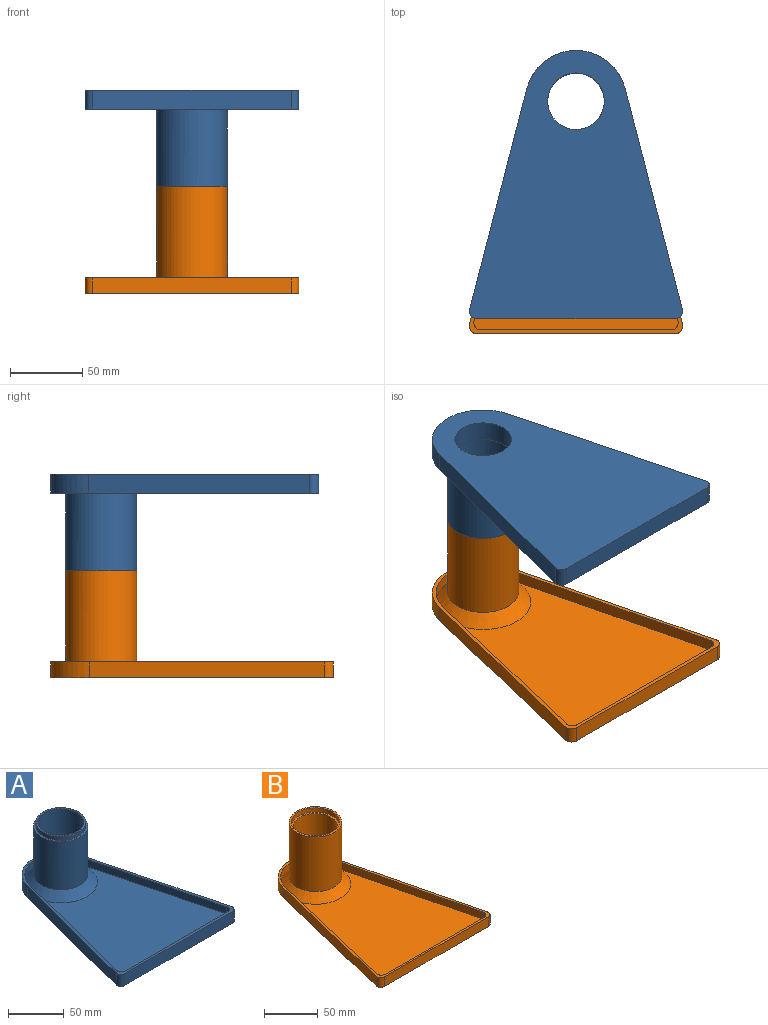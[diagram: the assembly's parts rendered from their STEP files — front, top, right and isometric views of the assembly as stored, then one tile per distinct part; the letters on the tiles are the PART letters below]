
ASSEMBLY  parts=2 mates=1
PART A: 25 faces, bbox 147.1x185x71 mm
  f0: plane 44.55x44.55mm, normal (0,0,1), area 196.3mm2, adj f19,f20
  f1: cylinder r=24.5mm len=53mm, axis (0,0,-1), area 8158.7mm2, adj f16,f17
  f2: plane 41.15x41.15mm, normal (0,0,1), area 135.3mm2, adj f14,f15
  f3: plane 152.52x39.5mm, normal (-0.97,0.25,0), area 2048.2mm2, adj f6,f7,f12,f23
  f4: plane 137.08x13mm, normal (0,-1,0), area 1782mm2, adj f7,f12,f23,f24
  f5: plane 152.52x39.5mm, normal (0.97,0.25,0), area 2048.2mm2, adj f6,f7,f12,f24
  f6: cylinder r=35mm len=67.76mm, axis (0,0,-1), area 1198.8mm2, adj f3,f5,f7,f12
  f7: plane 185x147.08mm, normal (0,0,-1), area 17390.7mm2, adj f3,f4,f5,f6,f14,f23,f24
  f8: plane 149.39x38.69mm, normal (-0.97,-0.25,0), area 1232.7mm2, adj f11,f12,f13,f16,f21
  f9: plane 130.62x8mm, normal (0,1,0), area 1045mm2, adj f12,f13,f21,f22
  f10: plane 149.39x38.69mm, normal (0.97,-0.25,0), area 1232.7mm2, adj f11,f12,f13,f16,f22
  f11: cylinder r=32.5mm len=62.92mm, axis (0,0,-1), area 642.2mm2, adj f8,f10,f12,f16
  f12: plane 185x147.08mm, normal (0,0,1), area 1401.2mm2, adj f3,f4,f5,f6,f8,f9,f10,f11
  f13: plane 150.11x140.62mm, normal (0,0,1), area 13809.8mm2, adj f8,f9,f10,f16,f21,f22
  f14: cylinder r=19.5mm len=39mm, axis (0,0,-1), area 1715.3mm2, adj f2,f7
  f15: cylinder r=20.57mm len=56.75mm, axis (0,0,-1), area 7336.4mm2, adj f2,f19
  f16: cone r=24.5mm half-angle=45deg, axis (0,0,-1), area 2105mm2, adj f1,f8,f10,f11,f13
  f17: plane 49x49mm, normal (0,0,1), area 291.8mm2, adj f1,f18
  f18: cylinder r=22.52mm len=45.05mm, axis (0,0,1), area 601.5mm2, adj f17,f20
  f19: cone r=20.57mm half-angle=45deg, axis (0,0,1), area 46mm2, adj f0,f15
  f20: cone r=22.27mm half-angle=45deg, axis (0,0,-1), area 49.8mm2, adj f0,f18
  f21: cylinder r=5mm len=8mm, axis (0,0,1), area 73mm2, adj f8,f9,f12,f13
  f22: cylinder r=5mm len=8mm, axis (0,0,-1), area 73mm2, adj f9,f10,f12,f13
  f23: cylinder r=5mm len=13mm, axis (0,0,1), area 118.6mm2, adj f3,f4,f7,f12
  f24: cylinder r=5mm len=13mm, axis (0,0,-1), area 118.6mm2, adj f4,f5,f7,f12
PART B: 23 faces, bbox 147.3x195x74 mm
  f0: plane 41.15x41.15mm, normal (0,0,1), area 135.3mm2, adj f12,f17
  f1: plane 162.1x39.49mm, normal (-0.97,0.24,0), area 1835.2mm2, adj f4,f5,f10,f21
  f2: plane 137.27x11mm, normal (0,-1,0), area 1510mm2, adj f5,f10,f21,f22
  f3: plane 162.1x39.49mm, normal (0.97,0.24,0), area 1835.2mm2, adj f4,f5,f10,f22
  f4: cylinder r=35mm len=68.01mm, axis (0,0,-1), area 1025.5mm2, adj f1,f3,f5,f10
  f5: plane 195x147.27mm, normal (0,0,-1), area 18480.7mm2, adj f1,f2,f3,f4,f12,f21,f22
  f6: plane 159.01x38.74mm, normal (-0.97,-0.24,0), area 1307.4mm2, adj f9,f10,f11,f18,f19
  f7: plane 130.91x8mm, normal (0,1,0), area 1047.3mm2, adj f10,f11,f19,f20
  f8: plane 159.01x38.74mm, normal (0.97,-0.24,0), area 1307.4mm2, adj f9,f10,f11,f18,f20
  f9: cylinder r=32.5mm len=63.15mm, axis (0,0,-1), area 649.3mm2, adj f6,f8,f10,f18
  f10: plane 195x147.27mm, normal (0,0,1), area 1449.9mm2, adj f1,f2,f3,f4,f6,f7,f8,f9
  f11: plane 159.63x140.91mm, normal (0,0,1), area 14851.7mm2, adj f6,f7,f8,f18,f19,f20
  f12: cylinder r=19.5mm len=39mm, axis (0,0,-1), area 1470.3mm2, adj f0,f5
  f13: cylinder r=24.5mm len=62.5mm, axis (0,0,-1), area 9621.1mm2, adj f15,f18
  f14: cylinder r=22.58mm len=45.15mm, axis (0,0,-1), area 709.2mm2, adj f15,f16
  f15: plane 49x49mm, normal (0,0,1), area 284.7mm2, adj f13,f14
  f16: plane 45.15x45.15mm, normal (0,0,1), area 271.1mm2, adj f14,f17
  f17: cylinder r=20.57mm len=57mm, axis (0,0,-1), area 7368.8mm2, adj f0,f16
  f18: cone r=24.5mm half-angle=45deg, axis (0,0,-1), area 2104.4mm2, adj f6,f8,f9,f11,f13
  f19: cylinder r=5mm len=8mm, axis (0,0,1), area 72.4mm2, adj f6,f7,f10,f11
  f20: cylinder r=5mm len=8mm, axis (0,0,-1), area 72.4mm2, adj f7,f8,f10,f11
  f21: cylinder r=5mm len=11mm, axis (0,0,1), area 99.5mm2, adj f1,f2,f5,f10
  f22: cylinder r=5mm len=11mm, axis (0,0,-1), area 99.5mm2, adj f2,f3,f5,f10
PLACE A rot(axis=(0,1,0),180deg) t=(0,0,140.4)mm
PLACE B at identity fixed
MATE fastened A.f18 <-> B.f13  axis (0,0,-1) through (0,0,73.9)mm
